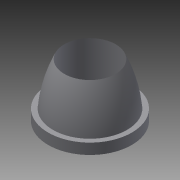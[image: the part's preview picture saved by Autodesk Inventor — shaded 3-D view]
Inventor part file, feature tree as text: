
AUTODESK INVENTOR PART (.ipt)
format: ipt  version: 2013 SP2 (Build 170200200, 200)  size: 100,864 bytes
history: native  units: mm
features: revolve x1
ambient origin geometry x8: Origin, YZ Plane, XZ Plane, XY Plane, X Axis, Y Axis, Z Axis, Center Point
bodies: Solid1 (feature_tree)
feature tree (1):
  revolve  "Revolution1"  [1 undecoded]
note: 1 required parameter value undecoded (feature->parameter linkage not recoverable at this tier; creation-order binding heuristic only, values carry confidence <= 0.55)
